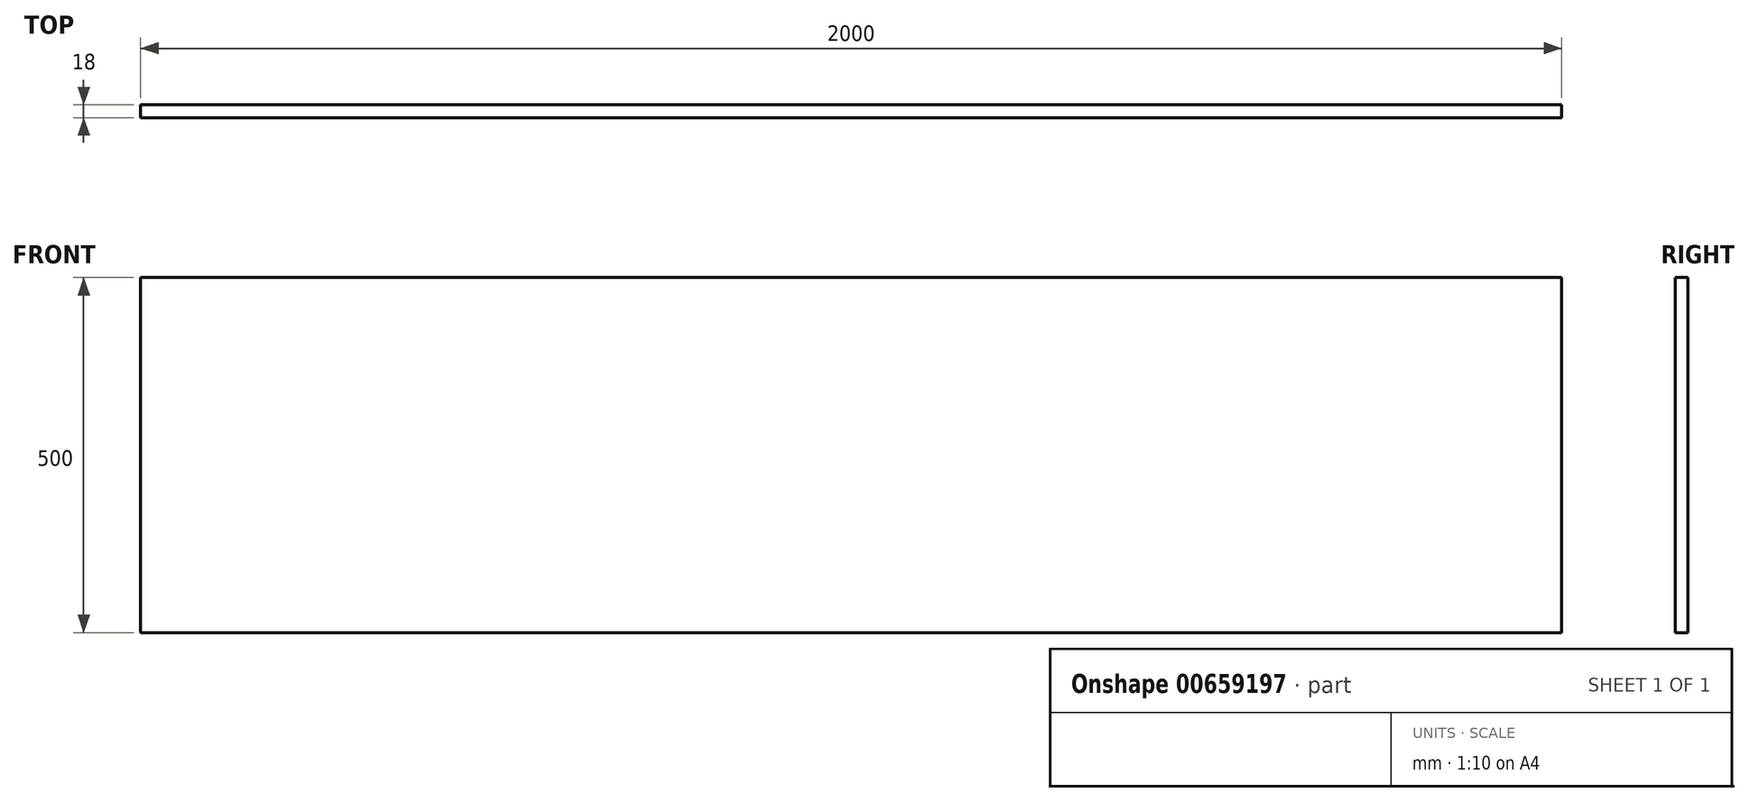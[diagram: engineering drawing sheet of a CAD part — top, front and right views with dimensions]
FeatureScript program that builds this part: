
annotation { "Feature Type Name" : "Feature", "Feature Type Description" : "" }
export const myFeature = defineFeature(function(context is Context, id is Id, definition is map)
    precondition{}
    {
        {
            var Q0;
            Q0=qCreatedBy(makeId("Front.planeOp"),FACE);
            var sketch = newSketch(context, id + "F0", { "sketchPlane" : qUnion([Q0])});
            skLineSegment(sketch, "E0.bottom", {"start": v(-411.05, 259.7) * mm, "end": v(1588.95, 259.7) * mm});
            skLineSegment(sketch, "E0.top", {"start": v(-411.05, -240.3) * mm, "end": v(1588.95, -240.3) * mm});
            skLineSegment(sketch, "E0.left", {"start": v(-411.05, 259.7) * mm, "end": v(-411.05, -240.3) * mm});
            skLineSegment(sketch, "E0.right", {"start": v(1588.95, 259.7) * mm, "end": v(1588.95, -240.3) * mm});
            skSolve(sketch);
        }
        {
            var Q0;
            Q0=makeQuery(id+"F0.imprint","IMPRINT",FACE,{"disambiguationData":[TD([[makeQuery(id+"F0.imprint","IMPRINT",EDGE,{"derivedFrom":sQuery(id+"F0.wireOp",EDGE,"E0.bottom")}),-1.0]])]});
            extrude(context, id + "F1", {"entities" : qUnion([Q0]), "endBound" : BoundingType.SYMMETRIC, "depth" : 18 * mm, "offsetDistance" : 25 * mm});
        }
    });
